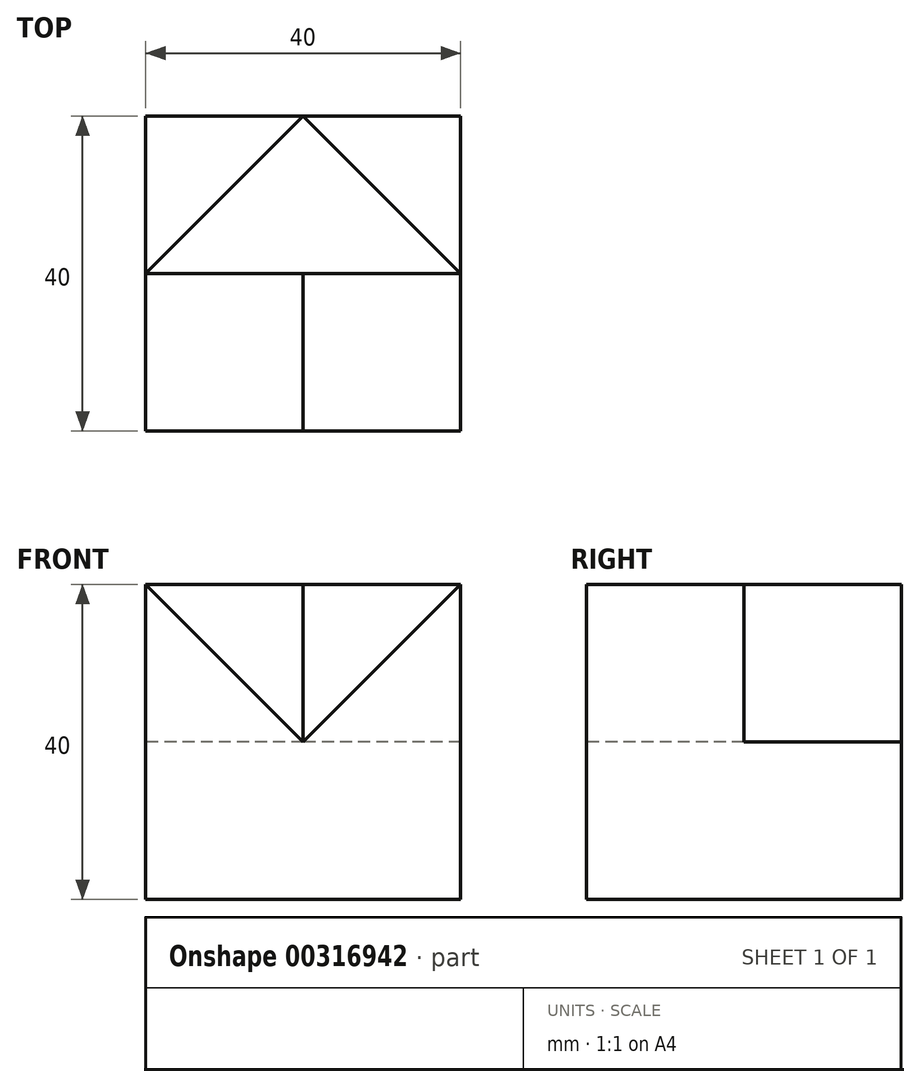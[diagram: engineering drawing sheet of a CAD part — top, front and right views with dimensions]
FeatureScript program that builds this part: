
annotation { "Feature Type Name" : "Feature", "Feature Type Description" : "" }
export const myFeature = defineFeature(function(context is Context, id is Id, definition is map)
    precondition{}
    {
        {
            var Q0;
            Q0=qCreatedBy(makeId("Top.planeOp"),FACE);
            var sketch = newSketch(context, id + "F0", { "sketchPlane" : qUnion([Q0])});
            skLineSegment(sketch, "E0.bottom", {"start": v(20, 20) * mm, "end": v(-20, 20) * mm});
            skLineSegment(sketch, "E0.top", {"start": v(20, -20) * mm, "end": v(-20, -20) * mm});
            skLineSegment(sketch, "E0.left", {"start": v(20, 20) * mm, "end": v(20, -20) * mm});
            skLineSegment(sketch, "E0.right", {"start": v(-20, 20) * mm, "end": v(-20, -20) * mm});
            skPoint(sketch, "E0.middle", {"position": v(0, 0) * mm});
            skSolve(sketch);
        }
        {
            var Q0;
            Q0=makeQuery(id+"F0.imprint","IMPRINT",FACE,{"disambiguationData":[TD([[makeQuery(id+"F0.imprint","IMPRINT",EDGE,{"derivedFrom":sQuery(id+"F0.wireOp",EDGE,"E0.bottom")}),1.0]])]});
            extrude(context, id + "F1", {"entities" : qUnion([Q0]), "depth" : 20 * mm});
        }
        {
            var Q0;
            Q0=makeQuery(id+"F1.opExtrude","SWEPT_FACE",FACE,{"disambiguationData":[OSD([sQuery(id+"F0.wireOp",EDGE,"E0.top")])]});
            var sketch = newSketch(context, id + "F2", { "sketchPlane" : qUnion([Q0])});
            skLineSegment(sketch, "E1", {"start": v(-20, 20) * mm, "end": v(-20, 40) * mm});
            skLineSegment(sketch, "E2", {"start": v(-20, 40) * mm, "end": v(0, 20) * mm});
            skLineSegment(sketch, "E3", {"start": v(20, 20) * mm, "end": v(20, 40) * mm});
            skLineSegment(sketch, "E4", {"start": v(20, 40) * mm, "end": v(0, 20) * mm});
            skSolve(sketch);
        }
        {
            var Q0;
            {var subQ0=sQuery(id+"F2.wireOp",EDGE,"E3");Q0=makeQuery(id+"F2.imprint","IMPRINT",FACE,{"disambiguationData":[TD([[makeQuery(id+"F2.imprint","IMPRINT",EDGE,{"derivedFrom":subQ0}),1.0]])]});}
            var Q1;
            {var subQ0=sQuery(id+"F2.wireOp",EDGE,"E1");Q1=makeQuery(id+"F2.imprint","IMPRINT",FACE,{"disambiguationData":[TD([[makeQuery(id+"F2.imprint","IMPRINT",EDGE,{"derivedFrom":subQ0}),-1.0]])]});}
            extrude(context, id + "F3", {"entities" : qUnion([Q0, Q1]), "operationType" : NewBodyOperationType.ADD, "oppositeDirection" : true, "depth" : 20 * mm});
        }
        {
            var Q0;
            Q0=makeQuery(id+"F1.opExtrude","CAP_FACE",FACE,{"disambiguationData":[OSD([sQuery(id+"F0.wireOp",EDGE,"E0.bottom"),sQuery(id+"F0.wireOp",EDGE,"E0.top"),sQuery(id+"F0.wireOp",EDGE,"E0.left"),sQuery(id+"F0.wireOp",EDGE,"E0.right")])],"isStart":false});
            var sketch = newSketch(context, id + "F4", { "sketchPlane" : qUnion([Q0])});
            skLineSegment(sketch, "E5", {"start": v(0, 20) * mm, "end": v(-20, 0) * mm});
            skLineSegment(sketch, "E6", {"start": v(-20, 0) * mm, "end": v(-20, 20) * mm});
            skLineSegment(sketch, "E7", {"start": v(-20, 20) * mm, "end": v(0, 20) * mm});
            skLineSegment(sketch, "E8", {"start": v(0, 20) * mm, "end": v(20, 0) * mm});
            skLineSegment(sketch, "E9", {"start": v(20, 0) * mm, "end": v(20, 20) * mm});
            skLineSegment(sketch, "E10", {"start": v(20, 20) * mm, "end": v(0, 20) * mm});
            skSolve(sketch);
        }
        {
            var Q0;
            Q0=makeQuery(id+"F4.imprint","IMPRINT",FACE,{"disambiguationData":[TD([[makeQuery(id+"F4.imprint","IMPRINT",EDGE,{"derivedFrom":sQuery(id+"F4.wireOp",EDGE,"E5")}),-1.0]])]});
            var Q1;
            Q1=makeQuery(id+"F4.imprint","IMPRINT",FACE,{"disambiguationData":[TD([[makeQuery(id+"F4.imprint","IMPRINT",EDGE,{"derivedFrom":sQuery(id+"F4.wireOp",EDGE,"E8")}),1.0]])]});
            extrude(context, id + "F5", {"entities" : qUnion([Q0, Q1]), "depth" : 20 * mm});
        }
    });
